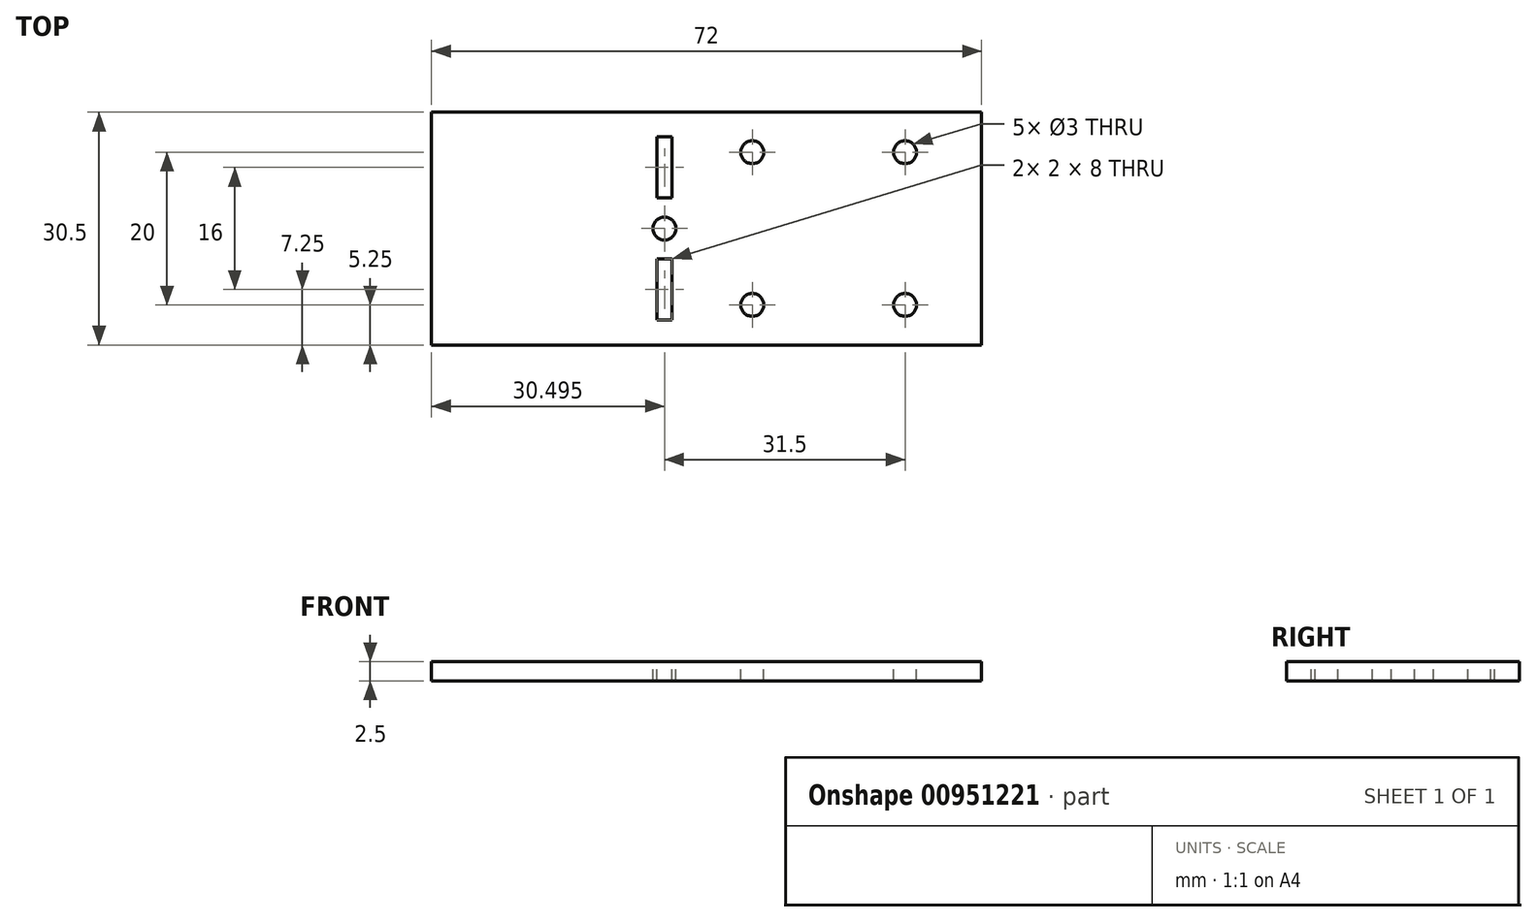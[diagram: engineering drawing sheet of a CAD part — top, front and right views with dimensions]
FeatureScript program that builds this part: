
annotation { "Feature Type Name" : "Feature", "Feature Type Description" : "" }
export const myFeature = defineFeature(function(context is Context, id is Id, definition is map)
    precondition{}
    {
        {
            var Q0;
            Q0=qCreatedBy(makeId("Top.planeOp"),FACE);
            var sketch = newSketch(context, id + "F0", { "sketchPlane" : qUnion([Q0])});
            skLineSegment(sketch, "E0.bottom", {"start": v(-34.65, 15.25) * mm, "end": v(37.35, 15.25) * mm});
            skLineSegment(sketch, "E0.top", {"start": v(-34.65, -15.25) * mm, "end": v(37.35, -15.25) * mm});
            skLineSegment(sketch, "E0.left", {"start": v(-34.65, 15.25) * mm, "end": v(-34.65, -15.25) * mm});
            skLineSegment(sketch, "E0.right", {"start": v(37.35, 15.25) * mm, "end": v(37.35, -15.25) * mm});
            skPoint(sketch, "E0.middle", {"position": v(1.35, 0) * mm});
            skCircle(sketch, "E1", {"center": v(7.35, 10) * mm, "radius": 1.5 * mm});
            skCircle(sketch, "E2", {"center": v(7.35, -10) * mm, "radius": 1.5 * mm});
            skCircle(sketch, "E3", {"center": v(27.35, -10) * mm, "radius": 1.5 * mm});
            skCircle(sketch, "E4", {"center": v(27.35, 10) * mm, "radius": 1.5 * mm});
            skLineSegment(sketch, "E5.bottom", {"start": v(-5.15, 4) * mm, "end": v(-3.15, 4) * mm});
            skLineSegment(sketch, "E5.top", {"start": v(-5.15, 12) * mm, "end": v(-3.15, 12) * mm});
            skLineSegment(sketch, "E5.left", {"start": v(-5.15, 4) * mm, "end": v(-5.15, 12) * mm});
            skLineSegment(sketch, "E5.right", {"start": v(-3.15, 4) * mm, "end": v(-3.15, 12) * mm});
            skPoint(sketch, "E5.middle", {"position": v(-4.15, 8) * mm});
            skLineSegment(sketch, "E6.bottom", {"start": v(-3.15, -12) * mm, "end": v(-5.15, -12) * mm});
            skLineSegment(sketch, "E6.top", {"start": v(-3.15, -4) * mm, "end": v(-5.15, -4) * mm});
            skLineSegment(sketch, "E6.left", {"start": v(-3.15, -12) * mm, "end": v(-3.15, -4) * mm});
            skLineSegment(sketch, "E6.right", {"start": v(-5.15, -12) * mm, "end": v(-5.15, -4) * mm});
            skPoint(sketch, "E6.middle", {"position": v(-4.15, -8) * mm});
            skLineSegment(sketch, "E7", {"start": v(1.35, 0) * mm, "end": v(-34.65, 0) * mm});
            skPoint(sketch, "E8", {"position": v(-4.15, 0) * mm});
            skCircle(sketch, "E9", {"center": v(-4.15, 0) * mm, "radius": 1.5 * mm});
            skSolve(sketch);
        }
        {
            var Q0;
            {var subQ0=sQuery(id+"F0.wireOp",EDGE,"E0.bottom");Q0=makeQuery(id+"F0.imprint","IMPRINT",FACE,{"disambiguationData":[TD([[makeQuery(id+"F0.imprint","IMPRINT",EDGE,{"derivedFrom":subQ0}),-1.0]])]});}
            extrude(context, id + "F1", {"entities" : qUnion([Q0]), "oppositeDirection" : true, "depth" : 2.5 * mm, "offsetDistance" : 25 * mm});
        }
    });
